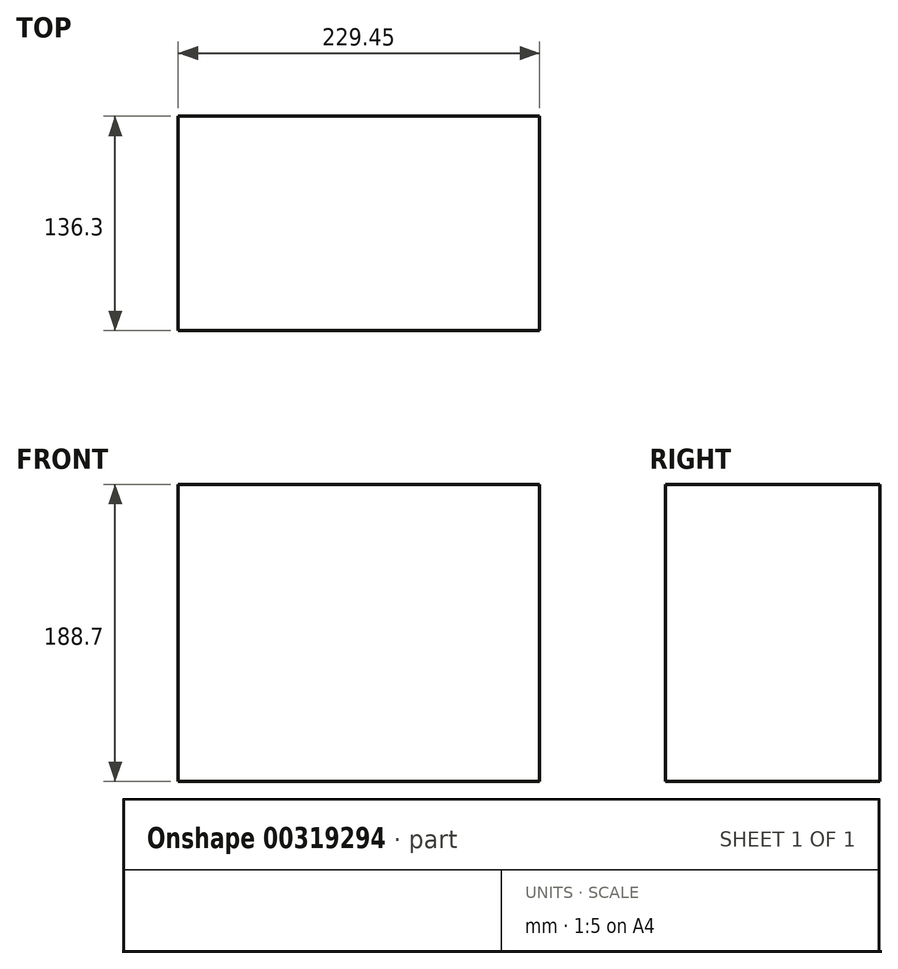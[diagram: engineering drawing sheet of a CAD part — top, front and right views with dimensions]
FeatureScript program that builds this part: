
annotation { "Feature Type Name" : "Feature", "Feature Type Description" : "" }
export const myFeature = defineFeature(function(context is Context, id is Id, definition is map)
    precondition{}
    {
        {
            var Q0;
            Q0=qCreatedBy(makeId("Top.planeOp"),FACE);
            var sketch = newSketch(context, id + "F0", { "sketchPlane" : qUnion([Q0])});
            skLineSegment(sketch, "E0.bottom", {"start": v(38.13, 145.87) * mm, "end": v(-191.32, 145.87) * mm});
            skLineSegment(sketch, "E0.top", {"start": v(38.13, 9.57) * mm, "end": v(-191.32, 9.57) * mm});
            skLineSegment(sketch, "E0.left", {"start": v(38.13, 145.87) * mm, "end": v(38.13, 9.57) * mm});
            skLineSegment(sketch, "E0.right", {"start": v(-191.32, 145.87) * mm, "end": v(-191.32, 9.57) * mm});
            skPoint(sketch, "E0.middle", {"position": v(-76.6, 77.72) * mm});
            skSolve(sketch);
        }
        {
            var Q0;
            Q0 = qSketchRegion(id + "F0", true);
            extrude(context, id + "F1", {"entities" : qUnion([Q0]), "depth" : 25.4 * mm});
        }
        {
            var Q0;
            Q0=makeQuery(id+"F1.opExtrude","CAP_FACE",FACE,{"disambiguationData":[OSD([sQuery(id+"F0.wireOp",EDGE,"E0.bottom"),sQuery(id+"F0.wireOp",EDGE,"E0.top"),sQuery(id+"F0.wireOp",EDGE,"E0.left"),sQuery(id+"F0.wireOp",EDGE,"E0.right")])],"isStart":false});
            extrude(context, id + "F2", {"entities" : qUnion([Q0]), "operationType" : NewBodyOperationType.ADD, "depth" : 102.8 * mm});
        }
        {
            var Q0;
            Q0=makeQuery(id+"F2.opExtrude","CAP_FACE",FACE,{"disambiguationData":[OSD([sQuery(id+"F0.wireOp",EDGE,"E0.bottom"),sQuery(id+"F0.wireOp",EDGE,"E0.top"),sQuery(id+"F0.wireOp",EDGE,"E0.left"),sQuery(id+"F0.wireOp",EDGE,"E0.right")])],"isStart":false});
            extrude(context, id + "F3", {"entities" : qUnion([Q0]), "operationType" : NewBodyOperationType.ADD, "oppositeDirection" : true, "depth" : 109.35 * mm});
        }
        {
            var Q0;
            Q0=makeQuery(id+"F2.opExtrude","CAP_FACE",FACE,{"disambiguationData":[OSD([sQuery(id+"F0.wireOp",EDGE,"E0.bottom"),sQuery(id+"F0.wireOp",EDGE,"E0.top"),sQuery(id+"F0.wireOp",EDGE,"E0.left"),sQuery(id+"F0.wireOp",EDGE,"E0.right")])],"isStart":false});
            extrude(context, id + "F4", {"entities" : qUnion([Q0]), "operationType" : NewBodyOperationType.ADD, "oppositeDirection" : true, "depth" : 188.7 * mm});
        }
    });
